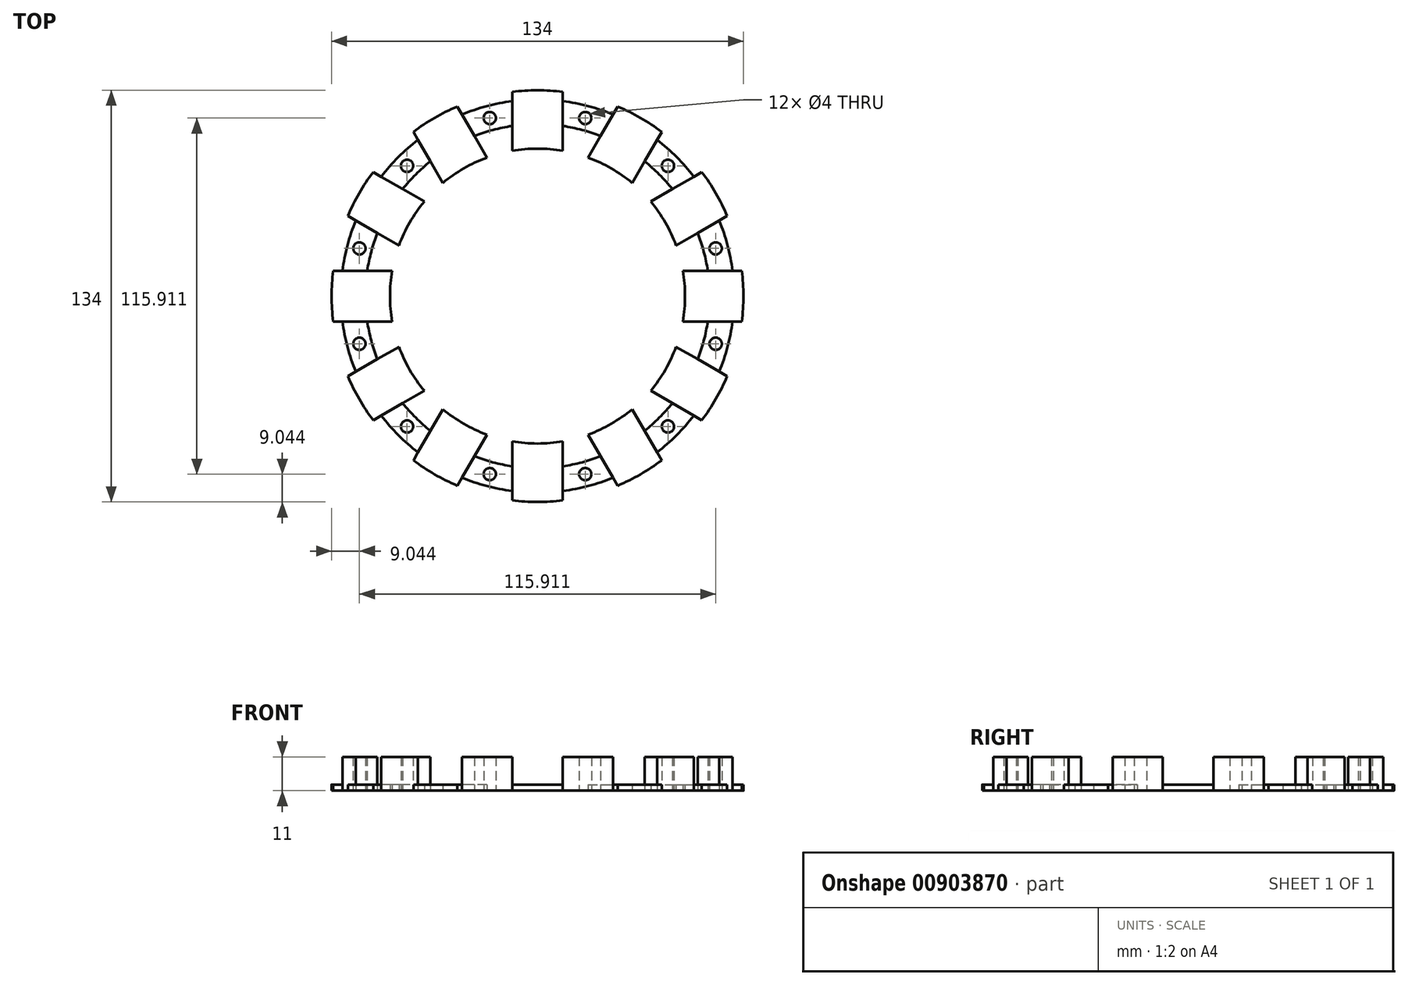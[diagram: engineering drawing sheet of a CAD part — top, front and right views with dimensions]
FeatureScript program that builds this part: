
annotation { "Feature Type Name" : "Feature", "Feature Type Description" : "" }
export const myFeature = defineFeature(function(context is Context, id is Id, definition is map)
    precondition{}
    {
        {
            var Q0;
            Q0=qCreatedBy(makeId("Top.planeOp"),FACE);
            var sketch = newSketch(context, id + "F0", { "sketchPlane" : qUnion([Q0])});
            skCircle(sketch, "E0", {"center": v(0, 0) * mm, "radius": 40 * mm, "construction": true});
            skCircle(sketch, "E1", {"center": v(0, 0) * mm, "radius": 60 * mm, "construction": true});
            skLineSegment(sketch, "E2.bottom", {"start": v(8.25, -39.14) * mm, "end": v(-8.25, -39.14) * mm});
            skLineSegment(sketch, "E2.top", {"start": v(8.25, -80.86) * mm, "end": v(-8.25, -80.86) * mm});
            skLineSegment(sketch, "E2.left", {"start": v(8.25, -39.14) * mm, "end": v(8.25, -80.86) * mm});
            skLineSegment(sketch, "E2.right", {"start": v(-8.25, -39.14) * mm, "end": v(-8.25, -80.86) * mm});
            skPoint(sketch, "E2.middle", {"position": v(0, -60) * mm});
            skLineSegment(sketch, "E3.1.0", {"start": v(26.71, -29.77) * mm, "end": v(47.57, -65.9) * mm});
            skLineSegment(sketch, "E3.1.1", {"start": v(12.43, -38.02) * mm, "end": v(33.29, -74.15) * mm});
            skLineSegment(sketch, "E3.1.2", {"start": v(47.57, -65.9) * mm, "end": v(33.29, -74.15) * mm});
            skLineSegment(sketch, "E3.1.3", {"start": v(26.71, -29.77) * mm, "end": v(12.43, -38.02) * mm});
            skLineSegment(sketch, "E3.2.0", {"start": v(38.02, -12.43) * mm, "end": v(74.15, -33.29) * mm});
            skLineSegment(sketch, "E3.2.1", {"start": v(29.77, -26.71) * mm, "end": v(65.9, -47.57) * mm});
            skLineSegment(sketch, "E3.2.2", {"start": v(74.15, -33.29) * mm, "end": v(65.9, -47.57) * mm});
            skLineSegment(sketch, "E3.2.3", {"start": v(38.02, -12.43) * mm, "end": v(29.77, -26.71) * mm});
            skLineSegment(sketch, "E3.3.0", {"start": v(39.14, 8.25) * mm, "end": v(80.86, 8.25) * mm});
            skLineSegment(sketch, "E3.3.1", {"start": v(39.14, -8.25) * mm, "end": v(80.86, -8.25) * mm});
            skLineSegment(sketch, "E3.3.2", {"start": v(80.86, 8.25) * mm, "end": v(80.86, -8.25) * mm});
            skLineSegment(sketch, "E3.3.3", {"start": v(39.14, 8.25) * mm, "end": v(39.14, -8.25) * mm});
            skLineSegment(sketch, "E3.4.0", {"start": v(29.77, 26.71) * mm, "end": v(65.9, 47.57) * mm});
            skLineSegment(sketch, "E3.4.1", {"start": v(38.02, 12.43) * mm, "end": v(74.15, 33.29) * mm});
            skLineSegment(sketch, "E3.4.2", {"start": v(65.9, 47.57) * mm, "end": v(74.15, 33.29) * mm});
            skLineSegment(sketch, "E3.4.3", {"start": v(29.77, 26.71) * mm, "end": v(38.02, 12.43) * mm});
            skLineSegment(sketch, "E3.5.0", {"start": v(12.43, 38.02) * mm, "end": v(33.29, 74.15) * mm});
            skLineSegment(sketch, "E3.5.1", {"start": v(26.71, 29.77) * mm, "end": v(47.57, 65.9) * mm});
            skLineSegment(sketch, "E3.5.2", {"start": v(33.29, 74.15) * mm, "end": v(47.57, 65.9) * mm});
            skLineSegment(sketch, "E3.5.3", {"start": v(12.43, 38.02) * mm, "end": v(26.71, 29.77) * mm});
            skLineSegment(sketch, "E3.6.0", {"start": v(-8.25, 39.14) * mm, "end": v(-8.25, 80.86) * mm});
            skLineSegment(sketch, "E3.6.1", {"start": v(8.25, 39.14) * mm, "end": v(8.25, 80.86) * mm});
            skLineSegment(sketch, "E3.6.2", {"start": v(-8.25, 80.86) * mm, "end": v(8.25, 80.86) * mm});
            skLineSegment(sketch, "E3.6.3", {"start": v(-8.25, 39.14) * mm, "end": v(8.25, 39.14) * mm});
            skLineSegment(sketch, "E3.7.0", {"start": v(-26.71, 29.77) * mm, "end": v(-47.57, 65.9) * mm});
            skLineSegment(sketch, "E3.7.1", {"start": v(-12.43, 38.02) * mm, "end": v(-33.29, 74.15) * mm});
            skLineSegment(sketch, "E3.7.2", {"start": v(-47.57, 65.9) * mm, "end": v(-33.29, 74.15) * mm});
            skLineSegment(sketch, "E3.7.3", {"start": v(-26.71, 29.77) * mm, "end": v(-12.43, 38.02) * mm});
            skLineSegment(sketch, "E3.8.0", {"start": v(-38.02, 12.43) * mm, "end": v(-74.15, 33.29) * mm});
            skLineSegment(sketch, "E3.8.1", {"start": v(-29.77, 26.71) * mm, "end": v(-65.9, 47.57) * mm});
            skLineSegment(sketch, "E3.8.2", {"start": v(-74.15, 33.29) * mm, "end": v(-65.9, 47.57) * mm});
            skLineSegment(sketch, "E3.8.3", {"start": v(-38.02, 12.43) * mm, "end": v(-29.77, 26.71) * mm});
            skLineSegment(sketch, "E3.9.0", {"start": v(-39.14, -8.25) * mm, "end": v(-80.86, -8.25) * mm});
            skLineSegment(sketch, "E3.9.1", {"start": v(-39.14, 8.25) * mm, "end": v(-80.86, 8.25) * mm});
            skLineSegment(sketch, "E3.9.2", {"start": v(-80.86, -8.25) * mm, "end": v(-80.86, 8.25) * mm});
            skLineSegment(sketch, "E3.9.3", {"start": v(-39.14, -8.25) * mm, "end": v(-39.14, 8.25) * mm});
            skLineSegment(sketch, "E3.10.0", {"start": v(-29.77, -26.71) * mm, "end": v(-65.9, -47.57) * mm});
            skLineSegment(sketch, "E3.10.1", {"start": v(-38.02, -12.43) * mm, "end": v(-74.15, -33.29) * mm});
            skLineSegment(sketch, "E3.10.2", {"start": v(-65.9, -47.57) * mm, "end": v(-74.15, -33.29) * mm});
            skLineSegment(sketch, "E3.10.3", {"start": v(-29.77, -26.71) * mm, "end": v(-38.02, -12.43) * mm});
            skLineSegment(sketch, "E3.11.0", {"start": v(-12.43, -38.02) * mm, "end": v(-33.29, -74.15) * mm});
            skLineSegment(sketch, "E3.11.1", {"start": v(-26.71, -29.77) * mm, "end": v(-47.57, -65.9) * mm});
            skLineSegment(sketch, "E3.11.2", {"start": v(-33.29, -74.15) * mm, "end": v(-47.57, -65.9) * mm});
            skLineSegment(sketch, "E3.11.3", {"start": v(-12.43, -38.02) * mm, "end": v(-26.71, -29.77) * mm});
            skCircle(sketch, "E4", {"center": v(0, 0) * mm, "radius": 81.28 * mm, "construction": true});
            skCircle(sketch, "E5", {"center": v(0, 0) * mm, "radius": 4.1 * mm});
            skLineSegment(sketch, "E6", {"start": v(0, 0) * mm, "end": v(-81.28, 0) * mm, "construction": true});
            skLineSegment(sketch, "E7", {"start": v(0, 0) * mm, "end": v(-78.51, 21.04) * mm, "construction": true});
            skCircle(sketch, "E8", {"center": v(0, 0) * mm, "radius": 62 * mm, "construction": true});
            skCircle(sketch, "E9", {"center": v(-57.96, 15.53) * mm, "radius": 2 * mm});
            skCircle(sketch, "E10.1.0", {"center": v(-57.96, -15.53) * mm, "radius": 2 * mm});
            skCircle(sketch, "E10.2.0", {"center": v(-42.43, -42.43) * mm, "radius": 2 * mm});
            skCircle(sketch, "E10.3.0", {"center": v(-15.53, -57.96) * mm, "radius": 2 * mm});
            skCircle(sketch, "E10.4.0", {"center": v(15.53, -57.96) * mm, "radius": 2 * mm});
            skCircle(sketch, "E10.5.0", {"center": v(42.43, -42.43) * mm, "radius": 2 * mm});
            skCircle(sketch, "E10.6.0", {"center": v(57.96, -15.53) * mm, "radius": 2 * mm});
            skCircle(sketch, "E10.7.0", {"center": v(57.96, 15.53) * mm, "radius": 2 * mm});
            skCircle(sketch, "E10.8.0", {"center": v(42.43, 42.43) * mm, "radius": 2 * mm});
            skCircle(sketch, "E10.9.0", {"center": v(15.53, 57.96) * mm, "radius": 2 * mm});
            skCircle(sketch, "E10.10.0", {"center": v(-15.53, 57.96) * mm, "radius": 2 * mm});
            skCircle(sketch, "E10.11.0", {"center": v(-42.43, 42.43) * mm, "radius": 2 * mm});
            skCircle(sketch, "E11", {"center": v(0, 0) * mm, "radius": 85 * mm});
            skCircle(sketch, "E12", {"center": v(0, 0) * mm, "radius": 87 * mm});
            skCircle(sketch, "E13", {"center": v(0, 0) * mm, "radius": 36 * mm});
            skCircle(sketch, "E14", {"center": v(0, 0) * mm, "radius": 67 * mm});
            skCircle(sketch, "E15", {"center": v(0, 0) * mm, "radius": 48 * mm});
            skCircle(sketch, "E16", {"center": v(0, 0) * mm, "radius": 56 * mm});
            skCircle(sketch, "E17", {"center": v(0, 0) * mm, "radius": 64 * mm});
            skSolve(sketch);
        }
        {
            var Q0;
            {var subQ0=sQuery(id+"F0.wireOp",EDGE,"E15");var subQ1=sQuery(id+"F0.wireOp",EDGE,"E3.4.0");var subQ2=makeQuery(id+"F0.imprint","INTERSECT",VERTEX,{"derivedFrom":[subQ1,subQ0]});Q0=makeQuery(id+"F0.imprint","IMPRINT",FACE,{"disambiguationData":[TD([[makeQuery(id+"F0.imprint","IMPRINT",EDGE,{"disambiguationData":[TD([[subQ2,-1.0]])],"derivedFrom":subQ1}),-1.0]])]});}
            var Q1;
            {var subQ0=sQuery(id+"F0.wireOp",EDGE,"E16");var subQ1=sQuery(id+"F0.wireOp",EDGE,"E3.4.0");var subQ2=makeQuery(id+"F0.imprint","INTERSECT",VERTEX,{"derivedFrom":[subQ1,subQ0]});Q1=makeQuery(id+"F0.imprint","IMPRINT",FACE,{"disambiguationData":[TD([[makeQuery(id+"F0.imprint","IMPRINT",EDGE,{"disambiguationData":[TD([[subQ2,-1.0]])],"derivedFrom":subQ1}),-1.0]])]});}
            var Q2;
            {var subQ0=sQuery(id+"F0.wireOp",EDGE,"E17");var subQ1=sQuery(id+"F0.wireOp",EDGE,"E3.4.0");var subQ2=makeQuery(id+"F0.imprint","INTERSECT",VERTEX,{"derivedFrom":[subQ1,subQ0]});Q2=makeQuery(id+"F0.imprint","IMPRINT",FACE,{"disambiguationData":[TD([[makeQuery(id+"F0.imprint","IMPRINT",EDGE,{"disambiguationData":[TD([[subQ2,-1.0]])],"derivedFrom":subQ1}),-1.0]])]});}
            var Q3;
            {var subQ0=sQuery(id+"F0.wireOp",EDGE,"E15");var subQ1=sQuery(id+"F0.wireOp",EDGE,"E3.3.0");var subQ2=makeQuery(id+"F0.imprint","INTERSECT",VERTEX,{"derivedFrom":[subQ1,subQ0]});Q3=makeQuery(id+"F0.imprint","IMPRINT",FACE,{"disambiguationData":[TD([[makeQuery(id+"F0.imprint","IMPRINT",EDGE,{"disambiguationData":[TD([[subQ2,-1.0]])],"derivedFrom":subQ1}),-1.0]])]});}
            var Q4;
            {var subQ0=sQuery(id+"F0.wireOp",EDGE,"E16");var subQ1=sQuery(id+"F0.wireOp",EDGE,"E3.3.0");var subQ2=makeQuery(id+"F0.imprint","INTERSECT",VERTEX,{"derivedFrom":[subQ1,subQ0]});Q4=makeQuery(id+"F0.imprint","IMPRINT",FACE,{"disambiguationData":[TD([[makeQuery(id+"F0.imprint","IMPRINT",EDGE,{"disambiguationData":[TD([[subQ2,-1.0]])],"derivedFrom":subQ1}),-1.0]])]});}
            var Q5;
            {var subQ0=sQuery(id+"F0.wireOp",EDGE,"E17");var subQ1=sQuery(id+"F0.wireOp",EDGE,"E3.3.0");var subQ2=makeQuery(id+"F0.imprint","INTERSECT",VERTEX,{"derivedFrom":[subQ1,subQ0]});Q5=makeQuery(id+"F0.imprint","IMPRINT",FACE,{"disambiguationData":[TD([[makeQuery(id+"F0.imprint","IMPRINT",EDGE,{"disambiguationData":[TD([[subQ2,-1.0]])],"derivedFrom":subQ1}),-1.0]])]});}
            var Q6;
            {var subQ0=sQuery(id+"F0.wireOp",EDGE,"E15");var subQ1=sQuery(id+"F0.wireOp",EDGE,"E3.2.0");var subQ2=makeQuery(id+"F0.imprint","INTERSECT",VERTEX,{"derivedFrom":[subQ1,subQ0]});Q6=makeQuery(id+"F0.imprint","IMPRINT",FACE,{"disambiguationData":[TD([[makeQuery(id+"F0.imprint","IMPRINT",EDGE,{"disambiguationData":[TD([[subQ2,-1.0]])],"derivedFrom":subQ1}),-1.0]])]});}
            var Q7;
            {var subQ0=sQuery(id+"F0.wireOp",EDGE,"E16");var subQ1=sQuery(id+"F0.wireOp",EDGE,"E3.2.0");var subQ2=makeQuery(id+"F0.imprint","INTERSECT",VERTEX,{"derivedFrom":[subQ1,subQ0]});Q7=makeQuery(id+"F0.imprint","IMPRINT",FACE,{"disambiguationData":[TD([[makeQuery(id+"F0.imprint","IMPRINT",EDGE,{"disambiguationData":[TD([[subQ2,-1.0]])],"derivedFrom":subQ1}),-1.0]])]});}
            var Q8;
            {var subQ0=sQuery(id+"F0.wireOp",EDGE,"E17");var subQ1=sQuery(id+"F0.wireOp",EDGE,"E3.2.0");var subQ2=makeQuery(id+"F0.imprint","INTERSECT",VERTEX,{"derivedFrom":[subQ1,subQ0]});Q8=makeQuery(id+"F0.imprint","IMPRINT",FACE,{"disambiguationData":[TD([[makeQuery(id+"F0.imprint","IMPRINT",EDGE,{"disambiguationData":[TD([[subQ2,-1.0]])],"derivedFrom":subQ1}),-1.0]])]});}
            var Q9;
            {var subQ0=sQuery(id+"F0.wireOp",EDGE,"E15");var subQ1=sQuery(id+"F0.wireOp",EDGE,"E3.1.0");var subQ2=makeQuery(id+"F0.imprint","INTERSECT",VERTEX,{"derivedFrom":[subQ1,subQ0]});Q9=makeQuery(id+"F0.imprint","IMPRINT",FACE,{"disambiguationData":[TD([[makeQuery(id+"F0.imprint","IMPRINT",EDGE,{"disambiguationData":[TD([[subQ2,-1.0]])],"derivedFrom":subQ1}),-1.0]])]});}
            var Q10;
            {var subQ0=sQuery(id+"F0.wireOp",EDGE,"E16");var subQ1=sQuery(id+"F0.wireOp",EDGE,"E3.1.0");var subQ2=makeQuery(id+"F0.imprint","INTERSECT",VERTEX,{"derivedFrom":[subQ1,subQ0]});Q10=makeQuery(id+"F0.imprint","IMPRINT",FACE,{"disambiguationData":[TD([[makeQuery(id+"F0.imprint","IMPRINT",EDGE,{"disambiguationData":[TD([[subQ2,-1.0]])],"derivedFrom":subQ1}),-1.0]])]});}
            var Q11;
            {var subQ0=sQuery(id+"F0.wireOp",EDGE,"E17");var subQ1=sQuery(id+"F0.wireOp",EDGE,"E3.1.0");var subQ2=makeQuery(id+"F0.imprint","INTERSECT",VERTEX,{"derivedFrom":[subQ1,subQ0]});Q11=makeQuery(id+"F0.imprint","IMPRINT",FACE,{"disambiguationData":[TD([[makeQuery(id+"F0.imprint","IMPRINT",EDGE,{"disambiguationData":[TD([[subQ2,-1.0]])],"derivedFrom":subQ1}),-1.0]])]});}
            var Q12;
            {var subQ0=sQuery(id+"F0.wireOp",EDGE,"E15");var subQ1=sQuery(id+"F0.wireOp",EDGE,"E2.left");var subQ2=makeQuery(id+"F0.imprint","INTERSECT",VERTEX,{"derivedFrom":[subQ1,subQ0]});Q12=makeQuery(id+"F0.imprint","IMPRINT",FACE,{"disambiguationData":[TD([[makeQuery(id+"F0.imprint","IMPRINT",EDGE,{"disambiguationData":[TD([[subQ2,-1.0]])],"derivedFrom":subQ1}),-1.0]])]});}
            var Q13;
            {var subQ0=sQuery(id+"F0.wireOp",EDGE,"E16");var subQ1=sQuery(id+"F0.wireOp",EDGE,"E2.left");var subQ2=makeQuery(id+"F0.imprint","INTERSECT",VERTEX,{"derivedFrom":[subQ1,subQ0]});Q13=makeQuery(id+"F0.imprint","IMPRINT",FACE,{"disambiguationData":[TD([[makeQuery(id+"F0.imprint","IMPRINT",EDGE,{"disambiguationData":[TD([[subQ2,-1.0]])],"derivedFrom":subQ1}),-1.0]])]});}
            var Q14;
            {var subQ0=sQuery(id+"F0.wireOp",EDGE,"E17");var subQ1=sQuery(id+"F0.wireOp",EDGE,"E2.left");var subQ2=makeQuery(id+"F0.imprint","INTERSECT",VERTEX,{"derivedFrom":[subQ1,subQ0]});Q14=makeQuery(id+"F0.imprint","IMPRINT",FACE,{"disambiguationData":[TD([[makeQuery(id+"F0.imprint","IMPRINT",EDGE,{"disambiguationData":[TD([[subQ2,-1.0]])],"derivedFrom":subQ1}),-1.0]])]});}
            var Q15;
            {var subQ0=sQuery(id+"F0.wireOp",EDGE,"E17");var subQ1=sQuery(id+"F0.wireOp",EDGE,"E3.11.0");var subQ2=makeQuery(id+"F0.imprint","INTERSECT",VERTEX,{"derivedFrom":[subQ1,subQ0]});Q15=makeQuery(id+"F0.imprint","IMPRINT",FACE,{"disambiguationData":[TD([[makeQuery(id+"F0.imprint","IMPRINT",EDGE,{"disambiguationData":[TD([[subQ2,-1.0]])],"derivedFrom":subQ1}),-1.0]])]});}
            var Q16;
            {var subQ0=sQuery(id+"F0.wireOp",EDGE,"E16");var subQ1=sQuery(id+"F0.wireOp",EDGE,"E3.11.0");var subQ2=makeQuery(id+"F0.imprint","INTERSECT",VERTEX,{"derivedFrom":[subQ1,subQ0]});Q16=makeQuery(id+"F0.imprint","IMPRINT",FACE,{"disambiguationData":[TD([[makeQuery(id+"F0.imprint","IMPRINT",EDGE,{"disambiguationData":[TD([[subQ2,-1.0]])],"derivedFrom":subQ1}),-1.0]])]});}
            var Q17;
            {var subQ0=sQuery(id+"F0.wireOp",EDGE,"E15");var subQ1=sQuery(id+"F0.wireOp",EDGE,"E3.11.0");var subQ2=makeQuery(id+"F0.imprint","INTERSECT",VERTEX,{"derivedFrom":[subQ1,subQ0]});Q17=makeQuery(id+"F0.imprint","IMPRINT",FACE,{"disambiguationData":[TD([[makeQuery(id+"F0.imprint","IMPRINT",EDGE,{"disambiguationData":[TD([[subQ2,-1.0]])],"derivedFrom":subQ1}),-1.0]])]});}
            var Q18;
            {var subQ0=sQuery(id+"F0.wireOp",EDGE,"E15");var subQ1=sQuery(id+"F0.wireOp",EDGE,"E3.10.0");var subQ2=makeQuery(id+"F0.imprint","INTERSECT",VERTEX,{"derivedFrom":[subQ1,subQ0]});Q18=makeQuery(id+"F0.imprint","IMPRINT",FACE,{"disambiguationData":[TD([[makeQuery(id+"F0.imprint","IMPRINT",EDGE,{"disambiguationData":[TD([[subQ2,-1.0]])],"derivedFrom":subQ1}),-1.0]])]});}
            var Q19;
            {var subQ0=sQuery(id+"F0.wireOp",EDGE,"E16");var subQ1=sQuery(id+"F0.wireOp",EDGE,"E3.10.0");var subQ2=makeQuery(id+"F0.imprint","INTERSECT",VERTEX,{"derivedFrom":[subQ1,subQ0]});Q19=makeQuery(id+"F0.imprint","IMPRINT",FACE,{"disambiguationData":[TD([[makeQuery(id+"F0.imprint","IMPRINT",EDGE,{"disambiguationData":[TD([[subQ2,-1.0]])],"derivedFrom":subQ1}),-1.0]])]});}
            var Q20;
            {var subQ0=sQuery(id+"F0.wireOp",EDGE,"E17");var subQ1=sQuery(id+"F0.wireOp",EDGE,"E3.10.0");var subQ2=makeQuery(id+"F0.imprint","INTERSECT",VERTEX,{"derivedFrom":[subQ1,subQ0]});Q20=makeQuery(id+"F0.imprint","IMPRINT",FACE,{"disambiguationData":[TD([[makeQuery(id+"F0.imprint","IMPRINT",EDGE,{"disambiguationData":[TD([[subQ2,-1.0]])],"derivedFrom":subQ1}),-1.0]])]});}
            var Q21;
            {var subQ0=sQuery(id+"F0.wireOp",EDGE,"E17");var subQ1=sQuery(id+"F0.wireOp",EDGE,"E3.9.0");var subQ2=makeQuery(id+"F0.imprint","INTERSECT",VERTEX,{"derivedFrom":[subQ1,subQ0]});Q21=makeQuery(id+"F0.imprint","IMPRINT",FACE,{"disambiguationData":[TD([[makeQuery(id+"F0.imprint","IMPRINT",EDGE,{"disambiguationData":[TD([[subQ2,-1.0]])],"derivedFrom":subQ1}),-1.0]])]});}
            var Q22;
            {var subQ0=sQuery(id+"F0.wireOp",EDGE,"E16");var subQ1=sQuery(id+"F0.wireOp",EDGE,"E3.9.0");var subQ2=makeQuery(id+"F0.imprint","INTERSECT",VERTEX,{"derivedFrom":[subQ1,subQ0]});Q22=makeQuery(id+"F0.imprint","IMPRINT",FACE,{"disambiguationData":[TD([[makeQuery(id+"F0.imprint","IMPRINT",EDGE,{"disambiguationData":[TD([[subQ2,-1.0]])],"derivedFrom":subQ1}),-1.0]])]});}
            var Q23;
            {var subQ0=sQuery(id+"F0.wireOp",EDGE,"E15");var subQ1=sQuery(id+"F0.wireOp",EDGE,"E3.9.0");var subQ2=makeQuery(id+"F0.imprint","INTERSECT",VERTEX,{"derivedFrom":[subQ1,subQ0]});Q23=makeQuery(id+"F0.imprint","IMPRINT",FACE,{"disambiguationData":[TD([[makeQuery(id+"F0.imprint","IMPRINT",EDGE,{"disambiguationData":[TD([[subQ2,-1.0]])],"derivedFrom":subQ1}),-1.0]])]});}
            var Q24;
            {var subQ0=sQuery(id+"F0.wireOp",EDGE,"E17");var subQ1=sQuery(id+"F0.wireOp",EDGE,"E3.8.0");var subQ2=makeQuery(id+"F0.imprint","INTERSECT",VERTEX,{"derivedFrom":[subQ1,subQ0]});Q24=makeQuery(id+"F0.imprint","IMPRINT",FACE,{"disambiguationData":[TD([[makeQuery(id+"F0.imprint","IMPRINT",EDGE,{"disambiguationData":[TD([[subQ2,-1.0]])],"derivedFrom":subQ1}),-1.0]])]});}
            var Q25;
            {var subQ0=sQuery(id+"F0.wireOp",EDGE,"E16");var subQ1=sQuery(id+"F0.wireOp",EDGE,"E3.8.0");var subQ2=makeQuery(id+"F0.imprint","INTERSECT",VERTEX,{"derivedFrom":[subQ1,subQ0]});Q25=makeQuery(id+"F0.imprint","IMPRINT",FACE,{"disambiguationData":[TD([[makeQuery(id+"F0.imprint","IMPRINT",EDGE,{"disambiguationData":[TD([[subQ2,-1.0]])],"derivedFrom":subQ1}),-1.0]])]});}
            var Q26;
            {var subQ0=sQuery(id+"F0.wireOp",EDGE,"E15");var subQ1=sQuery(id+"F0.wireOp",EDGE,"E3.8.0");var subQ2=makeQuery(id+"F0.imprint","INTERSECT",VERTEX,{"derivedFrom":[subQ1,subQ0]});Q26=makeQuery(id+"F0.imprint","IMPRINT",FACE,{"disambiguationData":[TD([[makeQuery(id+"F0.imprint","IMPRINT",EDGE,{"disambiguationData":[TD([[subQ2,-1.0]])],"derivedFrom":subQ1}),-1.0]])]});}
            var Q27;
            {var subQ0=sQuery(id+"F0.wireOp",EDGE,"E17");var subQ1=sQuery(id+"F0.wireOp",EDGE,"E3.7.0");var subQ2=makeQuery(id+"F0.imprint","INTERSECT",VERTEX,{"derivedFrom":[subQ1,subQ0]});Q27=makeQuery(id+"F0.imprint","IMPRINT",FACE,{"disambiguationData":[TD([[makeQuery(id+"F0.imprint","IMPRINT",EDGE,{"disambiguationData":[TD([[subQ2,-1.0]])],"derivedFrom":subQ1}),-1.0]])]});}
            var Q28;
            {var subQ0=sQuery(id+"F0.wireOp",EDGE,"E16");var subQ1=sQuery(id+"F0.wireOp",EDGE,"E3.7.0");var subQ2=makeQuery(id+"F0.imprint","INTERSECT",VERTEX,{"derivedFrom":[subQ1,subQ0]});Q28=makeQuery(id+"F0.imprint","IMPRINT",FACE,{"disambiguationData":[TD([[makeQuery(id+"F0.imprint","IMPRINT",EDGE,{"disambiguationData":[TD([[subQ2,-1.0]])],"derivedFrom":subQ1}),-1.0]])]});}
            var Q29;
            {var subQ0=sQuery(id+"F0.wireOp",EDGE,"E15");var subQ1=sQuery(id+"F0.wireOp",EDGE,"E3.7.0");var subQ2=makeQuery(id+"F0.imprint","INTERSECT",VERTEX,{"derivedFrom":[subQ1,subQ0]});Q29=makeQuery(id+"F0.imprint","IMPRINT",FACE,{"disambiguationData":[TD([[makeQuery(id+"F0.imprint","IMPRINT",EDGE,{"disambiguationData":[TD([[subQ2,-1.0]])],"derivedFrom":subQ1}),-1.0]])]});}
            var Q30;
            {var subQ0=sQuery(id+"F0.wireOp",EDGE,"E17");var subQ1=sQuery(id+"F0.wireOp",EDGE,"E3.6.0");var subQ2=makeQuery(id+"F0.imprint","INTERSECT",VERTEX,{"derivedFrom":[subQ1,subQ0]});Q30=makeQuery(id+"F0.imprint","IMPRINT",FACE,{"disambiguationData":[TD([[makeQuery(id+"F0.imprint","IMPRINT",EDGE,{"disambiguationData":[TD([[subQ2,-1.0]])],"derivedFrom":subQ1}),-1.0]])]});}
            var Q31;
            {var subQ0=sQuery(id+"F0.wireOp",EDGE,"E16");var subQ1=sQuery(id+"F0.wireOp",EDGE,"E3.6.0");var subQ2=makeQuery(id+"F0.imprint","INTERSECT",VERTEX,{"derivedFrom":[subQ1,subQ0]});Q31=makeQuery(id+"F0.imprint","IMPRINT",FACE,{"disambiguationData":[TD([[makeQuery(id+"F0.imprint","IMPRINT",EDGE,{"disambiguationData":[TD([[subQ2,-1.0]])],"derivedFrom":subQ1}),-1.0]])]});}
            var Q32;
            {var subQ0=sQuery(id+"F0.wireOp",EDGE,"E15");var subQ1=sQuery(id+"F0.wireOp",EDGE,"E3.6.0");var subQ2=makeQuery(id+"F0.imprint","INTERSECT",VERTEX,{"derivedFrom":[subQ1,subQ0]});Q32=makeQuery(id+"F0.imprint","IMPRINT",FACE,{"disambiguationData":[TD([[makeQuery(id+"F0.imprint","IMPRINT",EDGE,{"disambiguationData":[TD([[subQ2,-1.0]])],"derivedFrom":subQ1}),-1.0]])]});}
            var Q33;
            {var subQ0=sQuery(id+"F0.wireOp",EDGE,"E17");var subQ1=sQuery(id+"F0.wireOp",EDGE,"E3.5.0");var subQ2=makeQuery(id+"F0.imprint","INTERSECT",VERTEX,{"derivedFrom":[subQ1,subQ0]});Q33=makeQuery(id+"F0.imprint","IMPRINT",FACE,{"disambiguationData":[TD([[makeQuery(id+"F0.imprint","IMPRINT",EDGE,{"disambiguationData":[TD([[subQ2,-1.0]])],"derivedFrom":subQ1}),-1.0]])]});}
            var Q34;
            {var subQ0=sQuery(id+"F0.wireOp",EDGE,"E16");var subQ1=sQuery(id+"F0.wireOp",EDGE,"E3.5.0");var subQ2=makeQuery(id+"F0.imprint","INTERSECT",VERTEX,{"derivedFrom":[subQ1,subQ0]});Q34=makeQuery(id+"F0.imprint","IMPRINT",FACE,{"disambiguationData":[TD([[makeQuery(id+"F0.imprint","IMPRINT",EDGE,{"disambiguationData":[TD([[subQ2,-1.0]])],"derivedFrom":subQ1}),-1.0]])]});}
            var Q35;
            {var subQ0=sQuery(id+"F0.wireOp",EDGE,"E15");var subQ1=sQuery(id+"F0.wireOp",EDGE,"E3.5.0");var subQ2=makeQuery(id+"F0.imprint","INTERSECT",VERTEX,{"derivedFrom":[subQ1,subQ0]});Q35=makeQuery(id+"F0.imprint","IMPRINT",FACE,{"disambiguationData":[TD([[makeQuery(id+"F0.imprint","IMPRINT",EDGE,{"disambiguationData":[TD([[subQ2,-1.0]])],"derivedFrom":subQ1}),-1.0]])]});}
            extrude(context, id + "F1", {"entities" : qUnion([Q0, Q1, Q2, Q3, Q4, Q5, Q6, Q7, Q8, Q9, Q10, Q11, Q12, Q13, Q14, Q15, Q16, Q17, Q18, Q19, Q20, Q21, Q22, Q23, Q24, Q25, Q26, Q27, Q28, Q29, Q30, Q31, Q32, Q33, Q34, Q35]), "depth" : 2 * mm, "offsetDistance" : 25 * mm});
        }
        {
            var Q0;
            Q0=makeQuery(id+"F0.imprint","IMPRINT",FACE,{"disambiguationData":[TD([[makeQuery(id+"F0.imprint","IMPRINT",EDGE,{"derivedFrom":sQuery(id+"F0.wireOp",EDGE,"E10.9.0")}),-1.0]])]});
            var Q1;
            Q1=makeQuery(id+"F0.imprint","IMPRINT",FACE,{"disambiguationData":[TD([[makeQuery(id+"F0.imprint","IMPRINT",EDGE,{"derivedFrom":sQuery(id+"F0.wireOp",EDGE,"E10.8.0")}),-1.0]])]});
            var Q2;
            Q2=makeQuery(id+"F0.imprint","IMPRINT",FACE,{"disambiguationData":[TD([[makeQuery(id+"F0.imprint","IMPRINT",EDGE,{"derivedFrom":sQuery(id+"F0.wireOp",EDGE,"E10.7.0")}),-1.0]])]});
            var Q3;
            Q3=makeQuery(id+"F0.imprint","IMPRINT",FACE,{"disambiguationData":[TD([[makeQuery(id+"F0.imprint","IMPRINT",EDGE,{"derivedFrom":sQuery(id+"F0.wireOp",EDGE,"E10.6.0")}),-1.0]])]});
            var Q4;
            Q4=makeQuery(id+"F0.imprint","IMPRINT",FACE,{"disambiguationData":[TD([[makeQuery(id+"F0.imprint","IMPRINT",EDGE,{"derivedFrom":sQuery(id+"F0.wireOp",EDGE,"E10.5.0")}),-1.0]])]});
            var Q5;
            Q5=makeQuery(id+"F0.imprint","IMPRINT",FACE,{"disambiguationData":[TD([[makeQuery(id+"F0.imprint","IMPRINT",EDGE,{"derivedFrom":sQuery(id+"F0.wireOp",EDGE,"E10.4.0")}),-1.0]])]});
            var Q6;
            Q6=makeQuery(id+"F0.imprint","IMPRINT",FACE,{"disambiguationData":[TD([[makeQuery(id+"F0.imprint","IMPRINT",EDGE,{"derivedFrom":sQuery(id+"F0.wireOp",EDGE,"E10.3.0")}),-1.0]])]});
            var Q7;
            Q7=makeQuery(id+"F0.imprint","IMPRINT",FACE,{"disambiguationData":[TD([[makeQuery(id+"F0.imprint","IMPRINT",EDGE,{"derivedFrom":sQuery(id+"F0.wireOp",EDGE,"E10.2.0")}),-1.0]])]});
            var Q8;
            Q8=makeQuery(id+"F0.imprint","IMPRINT",FACE,{"disambiguationData":[TD([[makeQuery(id+"F0.imprint","IMPRINT",EDGE,{"derivedFrom":sQuery(id+"F0.wireOp",EDGE,"E10.1.0")}),-1.0]])]});
            var Q9;
            Q9=makeQuery(id+"F0.imprint","IMPRINT",FACE,{"disambiguationData":[TD([[makeQuery(id+"F0.imprint","IMPRINT",EDGE,{"derivedFrom":sQuery(id+"F0.wireOp",EDGE,"E9")}),-1.0]])]});
            var Q10;
            Q10=makeQuery(id+"F0.imprint","IMPRINT",FACE,{"disambiguationData":[TD([[makeQuery(id+"F0.imprint","IMPRINT",EDGE,{"derivedFrom":sQuery(id+"F0.wireOp",EDGE,"E10.11.0")}),-1.0]])]});
            var Q11;
            Q11=makeQuery(id+"F0.imprint","IMPRINT",FACE,{"disambiguationData":[TD([[makeQuery(id+"F0.imprint","IMPRINT",EDGE,{"derivedFrom":sQuery(id+"F0.wireOp",EDGE,"E10.10.0")}),-1.0]])]});
            extrude(context, id + "F2", {"entities" : qUnion([Q0, Q1, Q2, Q3, Q4, Q5, Q6, Q7, Q8, Q9, Q10, Q11]), "operationType" : NewBodyOperationType.ADD, "depth" : 11 * mm, "offsetDistance" : 25 * mm});
        }
    });
